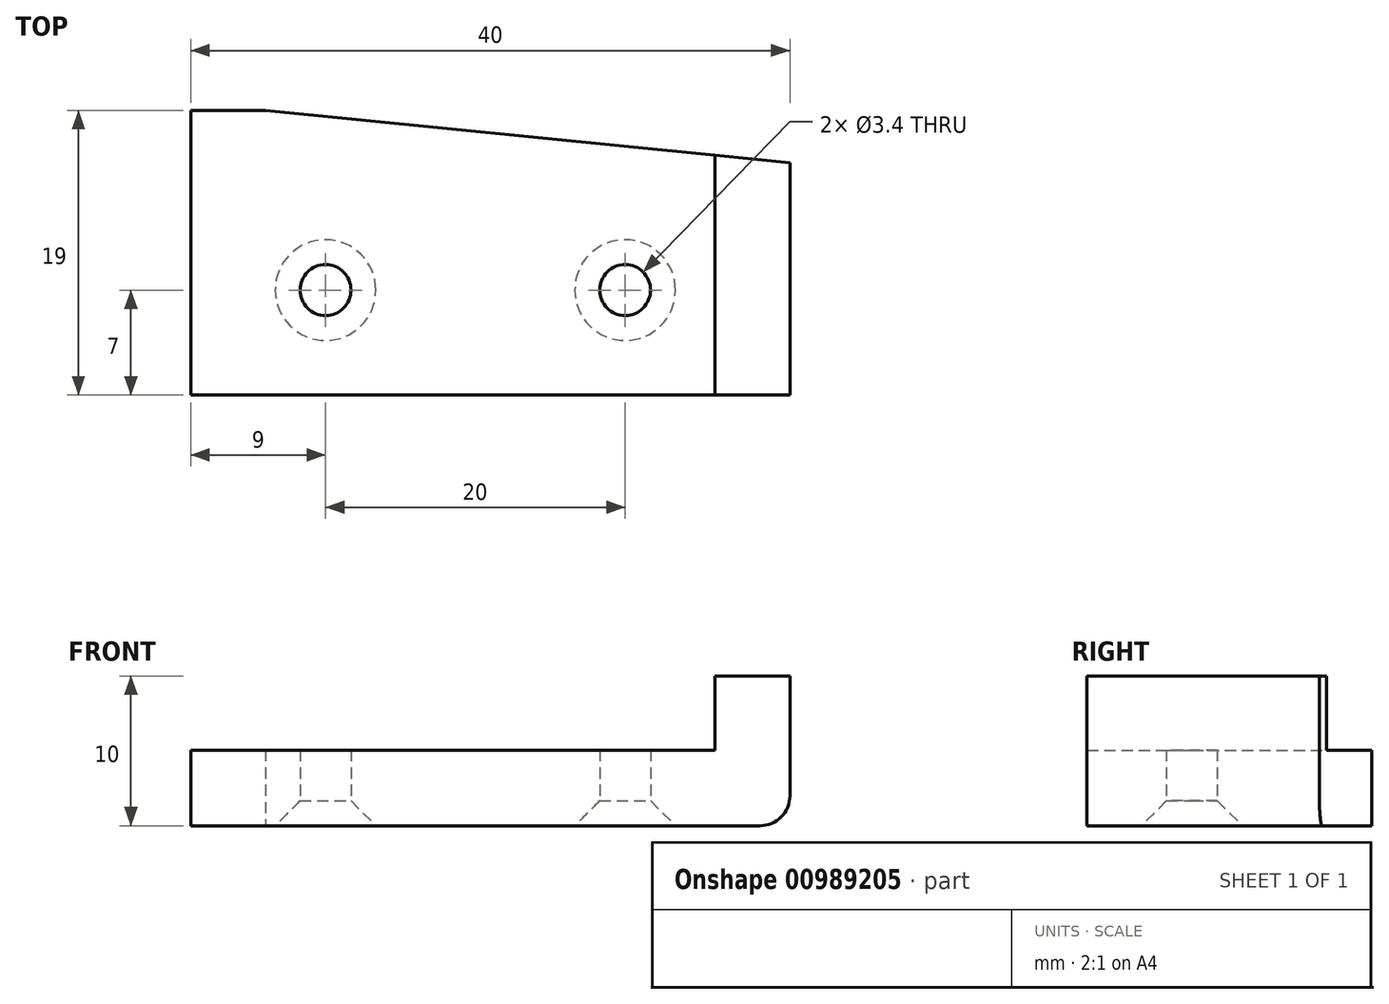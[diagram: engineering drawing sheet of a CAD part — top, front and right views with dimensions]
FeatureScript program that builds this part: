
annotation { "Feature Type Name" : "Feature", "Feature Type Description" : "" }
export const myFeature = defineFeature(function(context is Context, id is Id, definition is map)
    precondition{}
    {
        {
            var Q0;
            Q0=qCreatedBy(makeId("Front.planeOp"),FACE);
            var sketch = newSketch(context, id + "F0", { "sketchPlane" : qUnion([Q0])});
            skLineSegment(sketch, "E0", {"start": v(0, 0) * mm, "end": v(40, 0) * mm});
            skLineSegment(sketch, "E1", {"start": v(40, 0) * mm, "end": v(40, 10) * mm});
            skLineSegment(sketch, "E2", {"start": v(40, 10) * mm, "end": v(35, 10) * mm});
            skLineSegment(sketch, "E3", {"start": v(35, 10) * mm, "end": v(35, 5.04) * mm});
            skLineSegment(sketch, "E4", {"start": v(35, 5.04) * mm, "end": v(0, 5.04) * mm});
            skLineSegment(sketch, "E5", {"start": v(0, 5.04) * mm, "end": v(0, 0) * mm});
            skSolve(sketch);
        }
        {
            var Q0;
            Q0 = qSketchRegion(id + "F0", true);
            extrude(context, id + "F1", {"entities" : qUnion([Q0]), "depth" : 19 * mm, "offsetDistance" : 25 * mm});
        }
        {
            var Q0;
            Q0=makeQuery(id+"F1.opExtrude","SWEPT_FACE",FACE,{"disambiguationData":[OSD([sQuery(id+"F0.wireOp",EDGE,"E0")])]});
            var sketch = newSketch(context, id + "F2", { "sketchPlane" : qUnion([Q0])});
            skPoint(sketch, "E6", {"position": v(29, 12) * mm});
            skPoint(sketch, "E7", {"position": v(9, 12) * mm});
            skSolve(sketch);
        }
        {
            var Q0;
            Q0=sQuery(id+"F2.wireOp",VERTEX,"E7");
            var Q1;
            Q1=sQuery(id+"F2.wireOp",VERTEX,"E6");
            var Q2;
            Q2=makeQuery(id+"F1.opExtrude","SWEPT_BODY",BODY,{"disambiguationData":[OSD([sQuery(id+"F0.wireOp",EDGE,"E0"),sQuery(id+"F0.wireOp",EDGE,"E1"),sQuery(id+"F0.wireOp",EDGE,"E2"),sQuery(id+"F0.wireOp",EDGE,"E3"),sQuery(id+"F0.wireOp",EDGE,"E4"),sQuery(id+"F0.wireOp",EDGE,"E5")])]});
            hole(context, id + "F3", {"style" : HoleStyle.C_SINK, "endStyle" : HoleEndStyle.THROUGH, "standardTappedOrClearance" : lookupTablePath({ "fit" : "Normal", "standard" : "ISO", "size" : "M3", "type" : "Clearance" }), "standardBlindInLast" : lookupTablePath({ "fit" : "Normal", "standard" : "ISO", "engagement" : "75%", "pitch" : "0.5 mm", "size" : "M3", "type" : "Clearance & tapped" }), "holeDiameter" : 3.4 * mm, "cSinkDiameter" : 6.72 * mm, "cSinkAngle" : 90 * degree, "majorDiameter" : 4 * mm, "isTappedThrough" : true, "tappedDepth" : 5.6 * mm, "tapClearance" : 3, "startFromSketch" : true, "locations" : qUnion([Q0, Q1]), "scope" : qUnion([Q2])});
        }
        {
            var Q0;
            Q0=makeQuery(id+"F1.opExtrude","SWEPT_FACE",FACE,{"disambiguationData":[OSD([sQuery(id+"F0.wireOp",EDGE,"E0")])]});
            var sketch = newSketch(context, id + "F4", { "sketchPlane" : qUnion([Q0])});
            skPoint(sketch, "E8", {"position": v(40, 3.5) * mm});
            skPoint(sketch, "E9", {"position": v(5, 0) * mm});
            skLineSegment(sketch, "E10", {"start": v(5, 0) * mm, "end": v(40, 3.5) * mm});
            skLineSegment(sketch, "E11", {"start": v(40, 3.5) * mm, "end": v(40, 0) * mm});
            skLineSegment(sketch, "E12", {"start": v(5, 0) * mm, "end": v(40, 0) * mm});
            skSolve(sketch);
        }
        {
            var Q0;
            Q0 = qSketchRegion(id + "F4", true);
            extrude(context, id + "F5", {"entities" : qUnion([Q0]), "operationType" : NewBodyOperationType.REMOVE, "oppositeDirection" : true, "depth" : 25 * mm, "offsetDistance" : 25 * mm});
        }
        {
            var Q0;
            Q0=makeQuery(id+"F1.opExtrude","SWEPT_EDGE",EDGE,{"disambiguationData":[OSD([sQuery(id+"F0.wireOp",EDGE,"E0"),sQuery(id+"F0.wireOp",EDGE,"E1")])]});
            fillet(context, id + "F6", {"entities" : qUnion([Q0]), "radius" : 2 * mm, "tangentPropagation" : true, "allowEdgeOverflow" : false});
        }
    });
